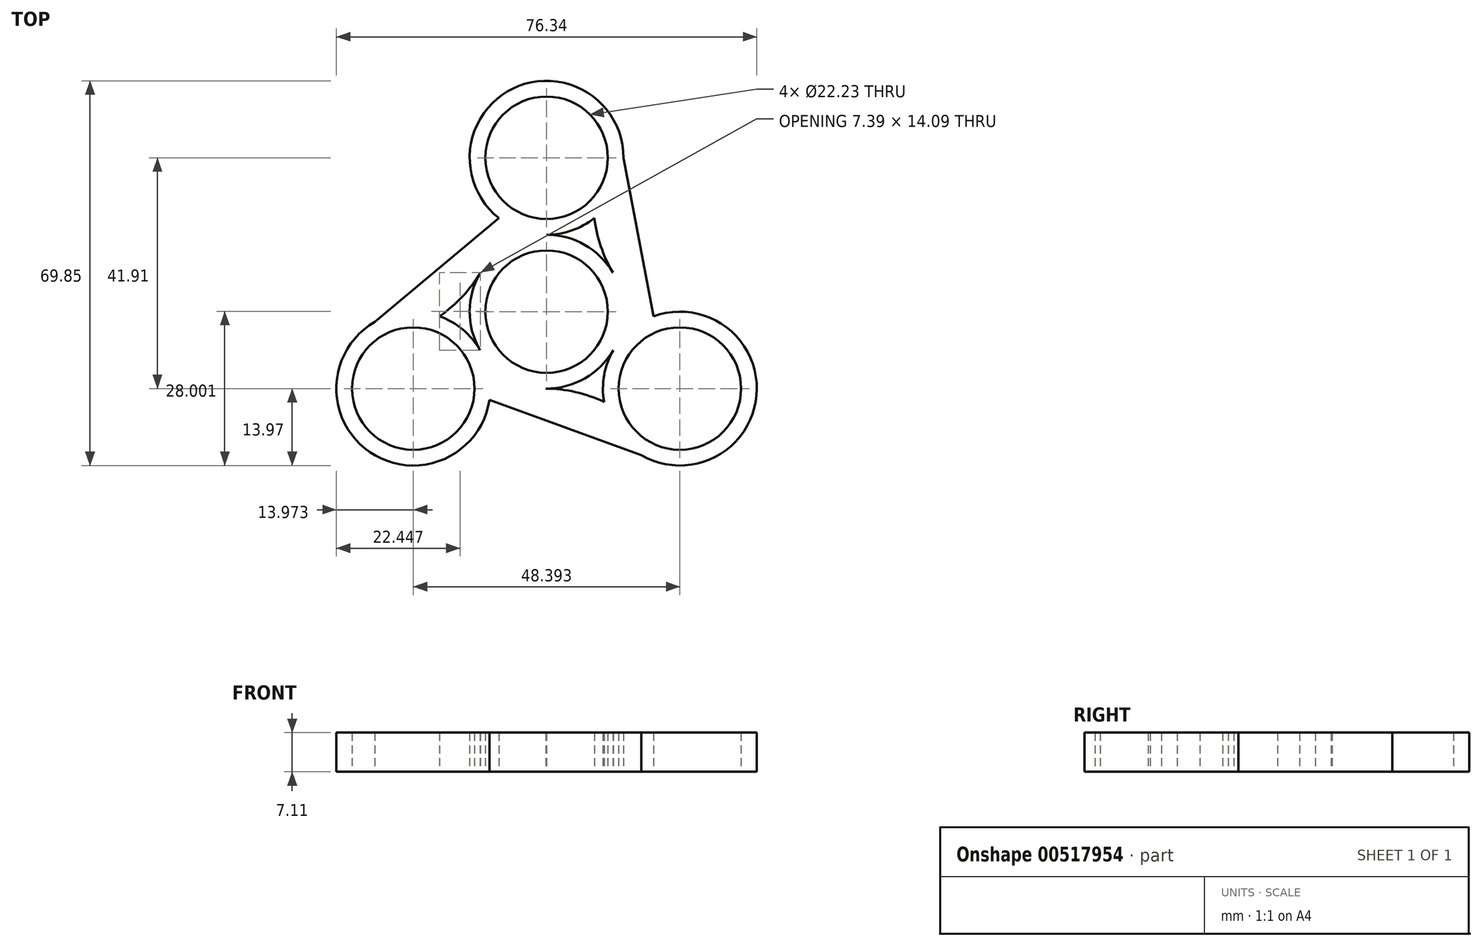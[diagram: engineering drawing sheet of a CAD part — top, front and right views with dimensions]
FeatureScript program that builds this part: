
annotation { "Feature Type Name" : "Feature", "Feature Type Description" : "" }
export const myFeature = defineFeature(function(context is Context, id is Id, definition is map)
    precondition{}
    {
        {
            var Q0;
            Q0=qCreatedBy(makeId("Top.planeOp"),FACE);
            var sketch = newSketch(context, id + "F0", { "sketchPlane" : qUnion([Q0])});
            skCircle(sketch, "E0", {"center": v(0, 0) * mm, "radius": 11.11 * mm});
            skCircle(sketch, "E1", {"center": v(0, 0) * mm, "radius": 13.97 * mm});
            skLineSegment(sketch, "E2", {"start": v(0, 0) * mm, "end": v(0, 27.94) * mm});
            skCircle(sketch, "E3", {"center": v(0, 27.94) * mm, "radius": 13.97 * mm});
            skCircle(sketch, "E4", {"center": v(0, 27.94) * mm, "radius": 11.11 * mm});
            skLineSegment(sketch, "E5", {"start": v(0, 0) * mm, "end": v(-24.2, -13.97) * mm});
            skLineSegment(sketch, "E6", {"start": v(0, 0) * mm, "end": v(24.2, -13.97) * mm});
            skCircle(sketch, "E7", {"center": v(-24.2, -13.97) * mm, "radius": 13.97 * mm});
            skCircle(sketch, "E8", {"center": v(-24.2, -13.97) * mm, "radius": 11.11 * mm});
            skCircle(sketch, "E9", {"center": v(24.2, -13.97) * mm, "radius": 13.97 * mm});
            skCircle(sketch, "E10", {"center": v(24.2, -13.97) * mm, "radius": 11.11 * mm});
            skLineSegment(sketch, "E11", {"start": v(0, 27.94) * mm, "end": v(-13.97, 27.94) * mm});
            skLineSegment(sketch, "E12", {"start": v(-24.2, -13.97) * mm, "end": v(-17.21, -26.07) * mm});
            skLineSegment(sketch, "E13", {"start": v(24.2, -13.97) * mm, "end": v(17.21, -26.07) * mm});
            skLineSegment(sketch, "E14", {"start": v(-12.1, -6.99) * mm, "end": v(-24.2, -13.97) * mm});
            skLineSegment(sketch, "E15", {"start": v(-24.2, -13.97) * mm, "end": v(-31.18, -1.87) * mm});
            skLineSegment(sketch, "E16", {"start": v(24.2, -13.97) * mm, "end": v(31.18, -1.87) * mm});
            skLineSegment(sketch, "E17", {"start": v(0, 27.94) * mm, "end": v(13.97, 27.94) * mm});
            skLineSegment(sketch, "E18", {"start": v(-24.2, -13.97) * mm, "end": v(-19.42, -0.84) * mm});
            skLineSegment(sketch, "E19", {"start": v(-8.68, 17) * mm, "end": v(0, 27.94) * mm});
            skArc(sketch, "E20", {"start": v(-19.42, -0.84) * mm, "mid": v(-12.14, 6.92) * mm, "end": v(-8.68, 17) * mm});
            skLineSegment(sketch, "E21", {"start": v(-24.2, -13.97) * mm, "end": v(-24.2, 0) * mm});
            skPoint(sketch, "E22.endSnap0", {"position": v(-4.34, 22.47) * mm});
            skArc(sketch, "E23.MirrorCS", {"start": v(19.42, -0.84) * mm, "mid": v(12.14, 6.92) * mm, "end": v(8.68, 17) * mm});
            skArc(sketch, "E24.MirrorCS", {"start": v(10.44, -16.4) * mm, "mid": v(0.07, -13.97) * mm, "end": v(-10.38, -16.01) * mm});
            skLineSegment(sketch, "E25", {"start": v(13.97, 27.94) * mm, "end": v(19.42, -0.84) * mm});
            skLineSegment(sketch, "E26", {"start": v(17.21, -26.07) * mm, "end": v(-10.38, -16.01) * mm});
            skLineSegment(sketch, "E27", {"start": v(-31.18, -1.87) * mm, "end": v(-8.68, 17) * mm});
            skSolve(sketch);
        }
        {
            var Q0;
            {var subQ0=sQuery(id+"F0.wireOp",EDGE,"E11");var subQ5=sQuery(id+"F0.wireOp",EDGE,"E4");var subQ6=makeQuery(id+"F0.imprint","INTERSECT",VERTEX,{"derivedFrom":[subQ5,subQ0]});Q0=makeQuery(id+"F0.imprint","IMPRINT",FACE,{"disambiguationData":[TD([[makeQuery(id+"F0.imprint","IMPRINT",EDGE,{"disambiguationData":[TD([[subQ6,1.0]])],"derivedFrom":subQ5}),-1.0]])]});}
            var Q1;
            {var subQ3=sQuery(id+"F0.wireOp",EDGE,"E15");var subQ5=sQuery(id+"F0.wireOp",EDGE,"E8");var subQ6=makeQuery(id+"F0.imprint","INTERSECT",VERTEX,{"derivedFrom":[subQ5,subQ3]});Q1=makeQuery(id+"F0.imprint","IMPRINT",FACE,{"disambiguationData":[TD([[makeQuery(id+"F0.imprint","IMPRINT",EDGE,{"disambiguationData":[TD([[subQ6,-1.0]])],"derivedFrom":subQ5}),-1.0]])]});}
            var Q2;
            {var subQ3=sQuery(id+"F0.wireOp",EDGE,"E16");var subQ5=sQuery(id+"F0.wireOp",EDGE,"E10");var subQ6=makeQuery(id+"F0.imprint","INTERSECT",VERTEX,{"derivedFrom":[subQ5,subQ3]});Q2=makeQuery(id+"F0.imprint","IMPRINT",FACE,{"disambiguationData":[TD([[makeQuery(id+"F0.imprint","IMPRINT",EDGE,{"disambiguationData":[TD([[subQ6,1.0]])],"derivedFrom":subQ5}),-1.0]])]});}
            var Q3;
            {var subQ0=sQuery(id+"F0.wireOp",EDGE,"E11");var subQ5=sQuery(id+"F0.wireOp",EDGE,"E4");var subQ6=makeQuery(id+"F0.imprint","INTERSECT",VERTEX,{"derivedFrom":[subQ5,subQ0]});Q3=makeQuery(id+"F0.imprint","IMPRINT",FACE,{"disambiguationData":[TD([[makeQuery(id+"F0.imprint","IMPRINT",EDGE,{"disambiguationData":[TD([[subQ6,-1.0]])],"derivedFrom":subQ5}),-1.0]])]});}
            var Q4;
            {var subQ3=sQuery(id+"F0.wireOp",EDGE,"E21");var subQ5=sQuery(id+"F0.wireOp",EDGE,"E8");var subQ7=makeQuery(id+"F0.imprint","INTERSECT",VERTEX,{"derivedFrom":[subQ5,subQ3]});Q4=makeQuery(id+"F0.imprint","IMPRINT",FACE,{"disambiguationData":[TD([[makeQuery(id+"F0.imprint","IMPRINT",EDGE,{"disambiguationData":[TD([[subQ7,-1.0]])],"derivedFrom":subQ5}),-1.0]])]});}
            var Q5;
            {var subQ1=sQuery(id+"F0.wireOp",EDGE,"E3");var subQ3=makeQuery(id+"F0.imprint","INTERSECT",VERTEX,{"derivedFrom":[subQ1,sQuery(id+"F0.wireOp",EDGE,"5e0eac27-506a-4d55-a6b8-50ddd9d8d8e10.MirrorCS")]});Q5=makeQuery(id+"F0.imprint","IMPRINT",FACE,{"disambiguationData":[TD([[makeQuery(id+"F0.imprint","IMPRINT",EDGE,{"disambiguationData":[TD([[subQ3,1.0]])],"derivedFrom":subQ1}),1.0]])]});}
            var Q6;
            {var subQ0=sQuery(id+"F0.wireOp",EDGE,"E9");var subQ6=makeQuery(id+"F0.imprint","INTERSECT",VERTEX,{"derivedFrom":[subQ0,sQuery(id+"F0.wireOp",EDGE,"5e0eac27-506a-4d55-a6b8-50ddd9d8d8e10.MirrorCS")]});Q6=makeQuery(id+"F0.imprint","IMPRINT",FACE,{"disambiguationData":[TD([[makeQuery(id+"F0.imprint","IMPRINT",EDGE,{"disambiguationData":[TD([[subQ6,-1.0]])],"derivedFrom":subQ0}),1.0]])]});}
            var Q7;
            {var subQ1=sQuery(id+"F0.wireOp",EDGE,"E9");var subQ4=makeQuery(id+"F0.imprint","INTERSECT",VERTEX,{"derivedFrom":[subQ1,sQuery(id+"F0.wireOp",EDGE,"E24.MirrorCS")]});Q7=makeQuery(id+"F0.imprint","IMPRINT",FACE,{"disambiguationData":[TD([[makeQuery(id+"F0.imprint","IMPRINT",EDGE,{"disambiguationData":[TD([[subQ4,-1.0]])],"derivedFrom":subQ1}),1.0]])]});}
            var Q8;
            {var subQ5=sQuery(id+"F0.wireOp",EDGE,"E7");var subQ7=makeQuery(id+"F0.imprint","INTERSECT",VERTEX,{"derivedFrom":[subQ5,sQuery(id+"F0.wireOp",EDGE,"E24.MirrorCS")]});Q8=makeQuery(id+"F0.imprint","IMPRINT",FACE,{"disambiguationData":[TD([[makeQuery(id+"F0.imprint","IMPRINT",EDGE,{"disambiguationData":[TD([[subQ7,1.0]])],"derivedFrom":subQ5}),1.0]])]});}
            var Q9;
            {var subQ0=sQuery(id+"F0.wireOp",EDGE,"E4");var subQ1=sQuery(id+"F0.wireOp",EDGE,"E2");var subQ2=makeQuery(id+"F0.imprint","INTERSECT",VERTEX,{"derivedFrom":[subQ1,subQ0]});Q9=makeQuery(id+"F0.imprint","IMPRINT",FACE,{"disambiguationData":[TD([[makeQuery(id+"F0.imprint","IMPRINT",EDGE,{"disambiguationData":[TD([[subQ2,1.0]])],"derivedFrom":subQ0}),-1.0]])]});}
            var Q10;
            {var subQ3=sQuery(id+"F0.wireOp",EDGE,"OxELbnh2-pf1s-LPYb-cjNd-jSZVnj8Dmi9T");var subQ5=sQuery(id+"F0.wireOp",EDGE,"E4");var subQ6=makeQuery(id+"F0.imprint","INTERSECT",VERTEX,{"derivedFrom":[subQ5,subQ3]});Q10=makeQuery(id+"F0.imprint","IMPRINT",FACE,{"disambiguationData":[TD([[makeQuery(id+"F0.imprint","IMPRINT",EDGE,{"disambiguationData":[TD([[subQ6,-1.0]])],"derivedFrom":subQ5}),-1.0]])]});}
            var Q11;
            {var subQ4=sQuery(id+"F0.wireOp",EDGE,"5e0eac27-506a-4d55-a6b8-50ddd9d8d8e10.MirrorCS");Q11=makeQuery(id+"F0.imprint","IMPRINT",FACE,{"disambiguationData":[TD([[makeQuery(id+"F0.imprint","IMPRINT",EDGE,{"derivedFrom":subQ4}),1.0]])]});}
            var Q12;
            {var subQ4=sQuery(id+"F0.wireOp",EDGE,"wTarZKbT-j9Fz-NUgE-Mupu-ReBFeg8jicUt");Q12=makeQuery(id+"F0.imprint","IMPRINT",FACE,{"disambiguationData":[TD([[makeQuery(id+"F0.imprint","IMPRINT",EDGE,{"derivedFrom":subQ4}),-1.0]])]});}
            var Q13;
            {var subQ6=sQuery(id+"F0.wireOp",EDGE,"fd0ed326-dc61-4633-886d-73886feb56c90.MirrorCS");Q13=makeQuery(id+"F0.imprint","IMPRINT",FACE,{"disambiguationData":[TD([[makeQuery(id+"F0.imprint","IMPRINT",EDGE,{"derivedFrom":subQ6}),-1.0]])]});}
            var Q14;
            {var subQ4=sQuery(id+"F0.wireOp",EDGE,"E5");var subQ6=sQuery(id+"F0.wireOp",EDGE,"E0");var subQ7=makeQuery(id+"F0.imprint","INTERSECT",VERTEX,{"derivedFrom":[subQ6,subQ4]});Q14=makeQuery(id+"F0.imprint","IMPRINT",FACE,{"disambiguationData":[TD([[makeQuery(id+"F0.imprint","IMPRINT",EDGE,{"disambiguationData":[TD([[subQ7,-1.0]])],"derivedFrom":subQ6}),-1.0]])]});}
            var Q15;
            {var subQ4=sQuery(id+"F0.wireOp",EDGE,"E5");var subQ6=sQuery(id+"F0.wireOp",EDGE,"E0");var subQ7=makeQuery(id+"F0.imprint","INTERSECT",VERTEX,{"derivedFrom":[subQ6,subQ4]});Q15=makeQuery(id+"F0.imprint","IMPRINT",FACE,{"disambiguationData":[TD([[makeQuery(id+"F0.imprint","IMPRINT",EDGE,{"disambiguationData":[TD([[subQ7,1.0]])],"derivedFrom":subQ6}),-1.0]])]});}
            var Q16;
            {var subQ0=sQuery(id+"F0.wireOp",EDGE,"E2");var subQ1=sQuery(id+"F0.wireOp",EDGE,"E0");var subQ2=makeQuery(id+"F0.imprint","INTERSECT",VERTEX,{"derivedFrom":[subQ1,subQ0]});Q16=makeQuery(id+"F0.imprint","IMPRINT",FACE,{"disambiguationData":[TD([[makeQuery(id+"F0.imprint","IMPRINT",EDGE,{"disambiguationData":[TD([[subQ2,1.0]])],"derivedFrom":subQ1}),-1.0]])]});}
            var Q17;
            {var subQ0=sQuery(id+"F0.wireOp",EDGE,"E18");var subQ5=sQuery(id+"F0.wireOp",EDGE,"E8");var subQ7=makeQuery(id+"F0.imprint","INTERSECT",VERTEX,{"derivedFrom":[subQ5,subQ0]});Q17=makeQuery(id+"F0.imprint","IMPRINT",FACE,{"disambiguationData":[TD([[makeQuery(id+"F0.imprint","IMPRINT",EDGE,{"disambiguationData":[TD([[subQ7,-1.0]])],"derivedFrom":subQ5}),-1.0]])]});}
            var Q18;
            {var subQ3=sQuery(id+"F0.wireOp",EDGE,"E18");var subQ5=sQuery(id+"F0.wireOp",EDGE,"E8");var subQ6=makeQuery(id+"F0.imprint","INTERSECT",VERTEX,{"derivedFrom":[subQ5,subQ3]});Q18=makeQuery(id+"F0.imprint","IMPRINT",FACE,{"disambiguationData":[TD([[makeQuery(id+"F0.imprint","IMPRINT",EDGE,{"disambiguationData":[TD([[subQ6,1.0]])],"derivedFrom":subQ5}),-1.0]])]});}
            var Q19;
            {var subQ4=sQuery(id+"F0.wireOp",EDGE,"E4");var subQ5=sQuery(id+"F0.wireOp",EDGE,"E2");var subQ6=makeQuery(id+"F0.imprint","INTERSECT",VERTEX,{"derivedFrom":[subQ5,subQ4]});Q19=makeQuery(id+"F0.imprint","IMPRINT",FACE,{"disambiguationData":[TD([[makeQuery(id+"F0.imprint","IMPRINT",EDGE,{"disambiguationData":[TD([[subQ6,-1.0]])],"derivedFrom":subQ4}),-1.0]])]});}
            var Q20;
            {var subQ0=sQuery(id+"F0.wireOp",EDGE,"E25");Q20=makeQuery(id+"F0.imprint","IMPRINT",FACE,{"disambiguationData":[TD([[makeQuery(id+"F0.imprint","IMPRINT",EDGE,{"derivedFrom":subQ0}),-1.0]])]});}
            var Q21;
            {var subQ0=sQuery(id+"F0.wireOp",EDGE,"E27");Q21=makeQuery(id+"F0.imprint","IMPRINT",FACE,{"disambiguationData":[TD([[makeQuery(id+"F0.imprint","IMPRINT",EDGE,{"derivedFrom":subQ0}),-1.0]])]});}
            var Q22;
            {var subQ0=sQuery(id+"F0.wireOp",EDGE,"E26");Q22=makeQuery(id+"F0.imprint","IMPRINT",FACE,{"disambiguationData":[TD([[makeQuery(id+"F0.imprint","IMPRINT",EDGE,{"derivedFrom":subQ0}),-1.0]])]});}
            var Q23;
            {var subQ0=sQuery(id+"F0.wireOp",EDGE,"E20");var subQ1=sQuery(id+"F0.wireOp",EDGE,"E1");var subQ2=makeQuery(id+"F0.imprint","INTERSECT",VERTEX,{"derivedFrom":[subQ1,subQ0]});Q23=makeQuery(id+"F0.imprint","IMPRINT",FACE,{"disambiguationData":[TD([[makeQuery(id+"F0.imprint","IMPRINT",EDGE,{"disambiguationData":[TD([[subQ2,1.0]])],"derivedFrom":subQ1}),-1.0]])]});}
            var Q24;
            {var subQ0=sQuery(id+"F0.wireOp",EDGE,"E23.MirrorCS");var subQ1=sQuery(id+"F0.wireOp",EDGE,"E1");var subQ2=makeQuery(id+"F0.imprint","INTERSECT",VERTEX,{"derivedFrom":[subQ1,subQ0]});Q24=makeQuery(id+"F0.imprint","IMPRINT",FACE,{"disambiguationData":[TD([[makeQuery(id+"F0.imprint","IMPRINT",EDGE,{"disambiguationData":[TD([[subQ2,1.0]])],"derivedFrom":subQ1}),-1.0]])]});}
            var Q25;
            {var subQ1=sQuery(id+"F0.wireOp",EDGE,"E1");var subQ3=sQuery(id+"F0.wireOp",EDGE,"E24.MirrorCS");var subQ4=makeQuery(id+"F0.imprint","INTERSECT",VERTEX,{"derivedFrom":[subQ1,subQ3]});Q25=makeQuery(id+"F0.imprint","IMPRINT",FACE,{"disambiguationData":[TD([[makeQuery(id+"F0.imprint","IMPRINT",EDGE,{"disambiguationData":[TD([[subQ4,-1.0]])],"derivedFrom":subQ3}),-1.0]])]});}
            extrude(context, id + "F1", {"entities" : qUnion([Q0, Q1, Q2, Q3, Q4, Q5, Q6, Q7, Q8, Q9, Q10, Q11, Q12, Q13, Q14, Q15, Q16, Q17, Q18, Q19, Q20, Q21, Q22, Q23, Q24, Q25]), "depth" : 7.11 * mm});
        }
    });
